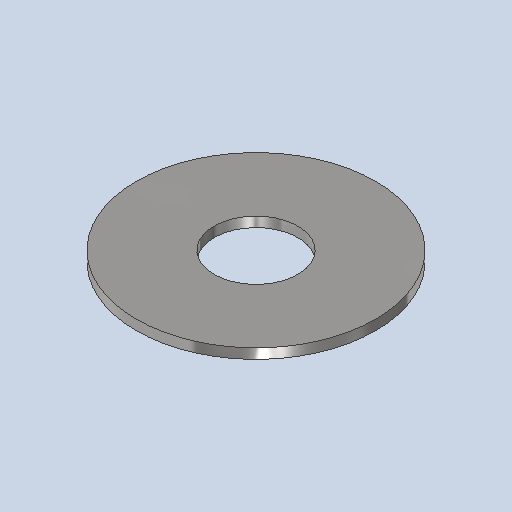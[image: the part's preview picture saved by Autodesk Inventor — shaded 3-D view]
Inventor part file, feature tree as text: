
AUTODESK INVENTOR PART (.ipt)
format: ipt  version: 2024.2 (Build 282272000, 272)  size: 245,248 bytes
history: native  units: mm
features: revolve x1, sketch x1
ambient origin geometry x8: Origin, YZ Plane, XZ Plane, XY Plane, X Axis, Y Axis, Z Axis, Center Point
bodies: Solid1 (feature_tree)
feature tree (2):
  revolve  "Revolution1"  [1 undecoded]
  sketch  "Sketch1"  dims[d5=90.0deg]
note: 1 required parameter value undecoded (feature->parameter linkage not recoverable at this tier; creation-order binding heuristic only, values carry confidence <= 0.55)
